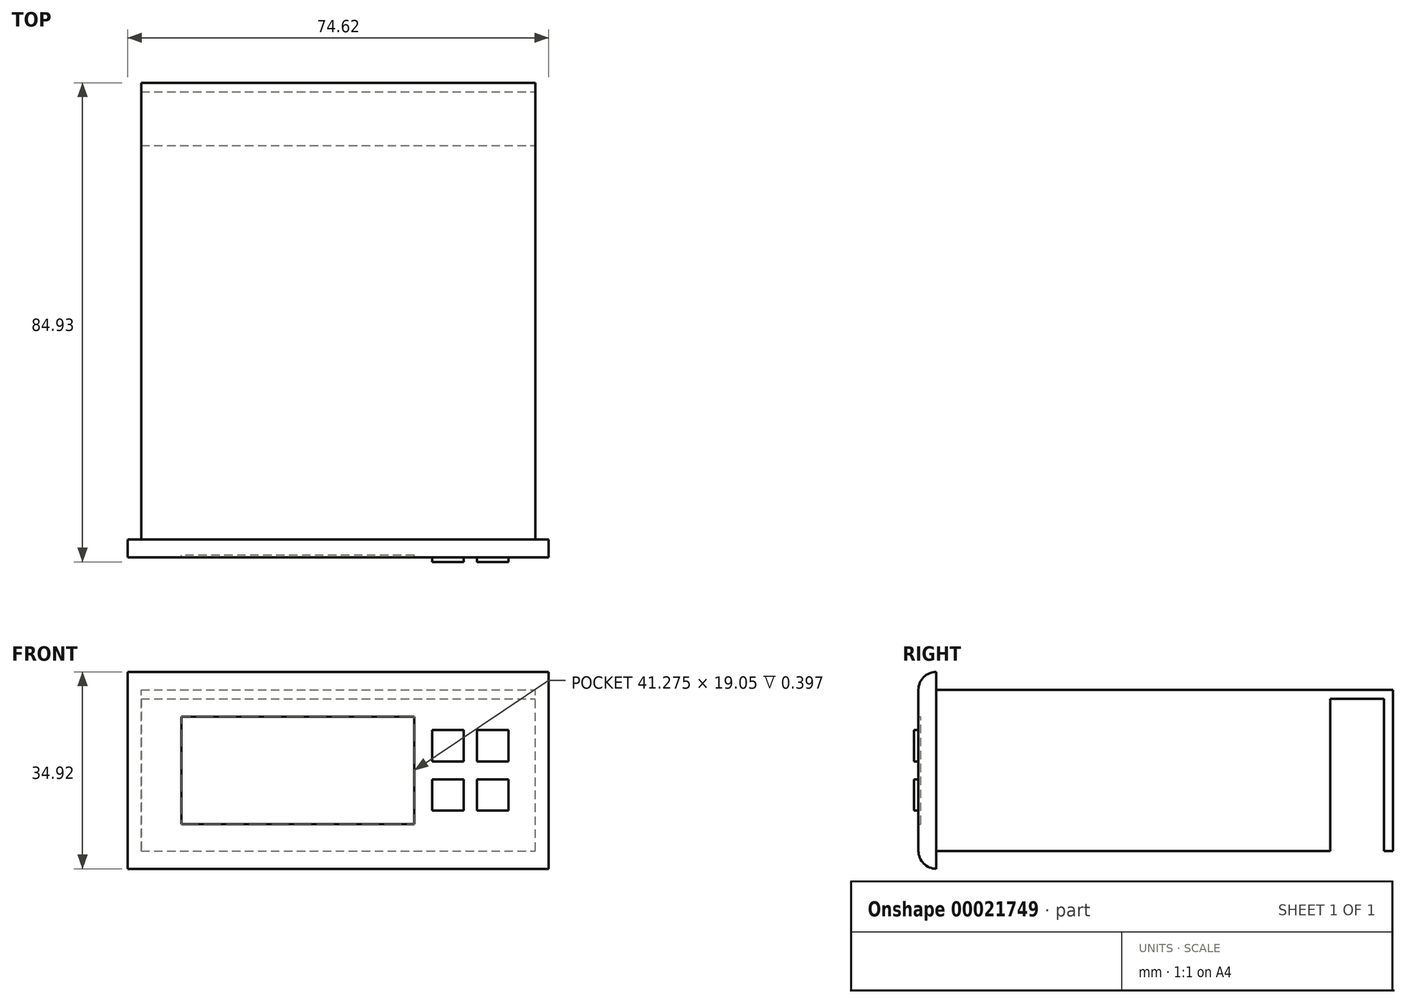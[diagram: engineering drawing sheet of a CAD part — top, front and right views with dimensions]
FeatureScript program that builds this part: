
annotation { "Feature Type Name" : "Feature", "Feature Type Description" : "" }
export const myFeature = defineFeature(function(context is Context, id is Id, definition is map)
    precondition{}
    {
        {
            var Q0;
            Q0=qCreatedBy(makeId("Front.planeOp"),FACE);
            var sketch = newSketch(context, id + "F0", { "sketchPlane" : qUnion([Q0])});
            skLineSegment(sketch, "E0.rect.bottom", {"start": v(37.3, 17.46) * mm, "end": v(-37.3, 17.46) * mm});
            skLineSegment(sketch, "E0.rect.top", {"start": v(37.3, -17.46) * mm, "end": v(-37.3, -17.46) * mm});
            skLineSegment(sketch, "E0.rect.left", {"start": v(37.3, 17.46) * mm, "end": v(37.3, -17.46) * mm});
            skLineSegment(sketch, "E0.rect.right", {"start": v(-37.3, 17.46) * mm, "end": v(-37.3, -17.46) * mm});
            skPoint(sketch, "E0.rect.middle", {"position": v(0, 0) * mm});
            skSolve(sketch);
        }
        {
            var Q0;
            Q0 = qSketchRegion(id + "F0", true);
            extrude(context, id + "F1", {"entities" : qUnion([Q0]), "oppositeDirection" : true, "depth" : 3.17 * mm});
        }
        {
            var Q0;
            Q0=makeQuery(id+"F1.opExtrude","CAP_FACE",FACE,{"disambiguationData":[OSD([sQuery(id+"F0.wireOp",EDGE,"E0.rect.bottom"),sQuery(id+"F0.wireOp",EDGE,"E0.rect.top"),sQuery(id+"F0.wireOp",EDGE,"E0.rect.left"),sQuery(id+"F0.wireOp",EDGE,"E0.rect.right")])],"isStart":false});
            var sketch = newSketch(context, id + "F2", { "sketchPlane" : qUnion([Q0])});
            skLineSegment(sketch, "E1.rect.bottom", {"start": v(34.93, -14.29) * mm, "end": v(-34.93, -14.29) * mm});
            skLineSegment(sketch, "E1.rect.top", {"start": v(34.93, 14.29) * mm, "end": v(-34.93, 14.29) * mm});
            skLineSegment(sketch, "E1.rect.left", {"start": v(34.93, -14.29) * mm, "end": v(34.93, 14.29) * mm});
            skLineSegment(sketch, "E1.rect.right", {"start": v(-34.93, -14.29) * mm, "end": v(-34.93, 14.29) * mm});
            skPoint(sketch, "E1.rect.middle", {"position": v(0, 0) * mm});
            skSolve(sketch);
        }
        {
            var Q0;
            Q0=makeQuery(id+"F2.imprint","IMPRINT",FACE,{"disambiguationData":[TD([[makeQuery(id+"F2.imprint","IMPRINT",EDGE,{"derivedFrom":sQuery(id+"F2.wireOp",EDGE,"E1.rect.bottom")}),-1.0]])]});
            extrude(context, id + "F3", {"entities" : qUnion([Q0]), "operationType" : NewBodyOperationType.ADD, "depth" : 80.96 * mm});
        }
        {
            var Q0;
            Q0=makeQuery(id+"F1.opExtrude","CAP_EDGE",EDGE,{"disambiguationData":[OSD([sQuery(id+"F0.wireOp",EDGE,"E0.rect.bottom")])],"isStart":true});
            var Q1;
            Q1=makeQuery(id+"F1.opExtrude","CAP_EDGE",EDGE,{"disambiguationData":[OSD([sQuery(id+"F0.wireOp",EDGE,"E0.rect.top")])],"isStart":true});
            fillet(context, id + "F4", {"entities" : qUnion([Q0, Q1]), "radius" : 3.17 * mm, "tangentPropagation" : true, "allowEdgeOverflow" : false});
        }
        {
            var Q0;
            Q0=makeQuery(id+"F1.opExtrude","CAP_FACE",FACE,{"disambiguationData":[OSD([sQuery(id+"F0.wireOp",EDGE,"E0.rect.bottom"),sQuery(id+"F0.wireOp",EDGE,"E0.rect.top"),sQuery(id+"F0.wireOp",EDGE,"E0.rect.left"),sQuery(id+"F0.wireOp",EDGE,"E0.rect.right")])],"isStart":true});
            var sketch = newSketch(context, id + "F5", { "sketchPlane" : qUnion([Q0])});
            skLineSegment(sketch, "E2.rect.bottom", {"start": v(13.5, -9.52) * mm, "end": v(-27.78, -9.52) * mm});
            skLineSegment(sketch, "E2.rect.top", {"start": v(13.5, 9.53) * mm, "end": v(-27.78, 9.53) * mm});
            skLineSegment(sketch, "E2.rect.left", {"start": v(13.5, -9.52) * mm, "end": v(13.5, 9.53) * mm});
            skLineSegment(sketch, "E2.rect.right", {"start": v(-27.78, -9.52) * mm, "end": v(-27.78, 9.53) * mm});
            skPoint(sketch, "E2.rect.middle", {"position": v(-7.14, 0) * mm});
            skSolve(sketch);
        }
        {
            var Q0;
            Q0 = qSketchRegion(id + "F5", true);
            extrude(context, id + "F6", {"entities" : qUnion([Q0]), "operationType" : NewBodyOperationType.REMOVE, "oppositeDirection" : true, "depth" : 0.4 * mm});
        }
        {
            var Q0;
            Q0=makeQuery(id+"F1.opExtrude","CAP_FACE",FACE,{"disambiguationData":[OSD([sQuery(id+"F0.wireOp",EDGE,"E0.rect.bottom"),sQuery(id+"F0.wireOp",EDGE,"E0.rect.top"),sQuery(id+"F0.wireOp",EDGE,"E0.rect.left"),sQuery(id+"F0.wireOp",EDGE,"E0.rect.right")])],"isStart":true});
            var sketch = newSketch(context, id + "F7", { "sketchPlane" : qUnion([Q0])});
            skLineSegment(sketch, "E3.rect.bottom", {"start": v(22.23, 1.59) * mm, "end": v(16.67, 1.59) * mm});
            skLineSegment(sketch, "E3.rect.top", {"start": v(22.23, 7.14) * mm, "end": v(16.67, 7.14) * mm});
            skLineSegment(sketch, "E3.rect.left", {"start": v(22.23, 1.59) * mm, "end": v(22.23, 7.14) * mm});
            skLineSegment(sketch, "E3.rect.right", {"start": v(16.67, 1.59) * mm, "end": v(16.67, 7.14) * mm});
            skPoint(sketch, "E3.rect.middle", {"position": v(19.45, 4.37) * mm});
            skLineSegment(sketch, "E4.1.0.0", {"start": v(24.6, 1.59) * mm, "end": v(24.6, 7.14) * mm});
            skLineSegment(sketch, "E4.1.0.1", {"start": v(30.16, 1.59) * mm, "end": v(24.6, 1.59) * mm});
            skLineSegment(sketch, "E4.1.0.2", {"start": v(30.16, 1.59) * mm, "end": v(30.16, 7.14) * mm});
            skLineSegment(sketch, "E4.1.0.3", {"start": v(30.16, 7.14) * mm, "end": v(24.6, 7.14) * mm});
            skLineSegment(sketch, "E4.direction1", {"start": v(16.67, 1.59) * mm, "end": v(22.23, 1.59) * mm, "construction": true});
            skLineSegment(sketch, "E5.MirrorCS", {"start": v(16.67, -1.59) * mm, "end": v(16.67, -7.14) * mm});
            skLineSegment(sketch, "E6.MirrorCS", {"start": v(22.23, -7.14) * mm, "end": v(16.67, -7.14) * mm});
            skLineSegment(sketch, "E7.MirrorCS", {"start": v(22.23, -1.59) * mm, "end": v(16.67, -1.59) * mm});
            skLineSegment(sketch, "E8.MirrorCS", {"start": v(30.16, -7.14) * mm, "end": v(24.6, -7.14) * mm});
            skLineSegment(sketch, "E9.MirrorCS", {"start": v(16.67, -7.14) * mm, "end": v(16.67, -1.59) * mm});
            skLineSegment(sketch, "E10.MirrorCS", {"start": v(22.23, -1.59) * mm, "end": v(22.23, -7.14) * mm});
            skLineSegment(sketch, "E11.MirrorCS", {"start": v(30.16, -1.59) * mm, "end": v(24.6, -1.59) * mm});
            skLineSegment(sketch, "E12.MirrorCS", {"start": v(30.16, -7.14) * mm, "end": v(30.16, -1.59) * mm});
            skLineSegment(sketch, "E13.MirrorCS", {"start": v(24.6, -1.59) * mm, "end": v(24.6, -7.14) * mm});
            skLineSegment(sketch, "E14.MirrorCS", {"start": v(16.67, -1.59) * mm, "end": v(22.23, -1.59) * mm});
            skPoint(sketch, "E15.MirrorP", {"position": v(19.45, -4.37) * mm});
            skSolve(sketch);
        }
        {
            var Q0;
            Q0=makeQuery(id+"F7.imprint","IMPRINT",FACE,{"disambiguationData":[TD([[makeQuery(id+"F7.imprint","IMPRINT",EDGE,{"derivedFrom":sQuery(id+"F7.wireOp",EDGE,"E3.rect.bottom")}),-1.0]])]});
            var Q1;
            Q1=makeQuery(id+"F7.imprint","IMPRINT",FACE,{"disambiguationData":[TD([[makeQuery(id+"F7.imprint","IMPRINT",EDGE,{"derivedFrom":sQuery(id+"F7.wireOp",EDGE,"E4.1.0.0")}),-1.0]])]});
            var Q2;
            Q2=makeQuery(id+"F7.imprint","IMPRINT",FACE,{"disambiguationData":[TD([[makeQuery(id+"F7.imprint","IMPRINT",EDGE,{"derivedFrom":sQuery(id+"F7.wireOp",EDGE,"E8.MirrorCS")}),-1.0]])]});
            var Q3;
            Q3=makeQuery(id+"F7.imprint","IMPRINT",FACE,{"disambiguationData":[TD([[makeQuery(id+"F7.imprint","IMPRINT",EDGE,{"derivedFrom":sQuery(id+"F7.wireOp",EDGE,"E6.MirrorCS")}),-1.0]])]});
            extrude(context, id + "F8", {"entities" : qUnion([Q0, Q1, Q2, Q3]), "operationType" : NewBodyOperationType.ADD, "depth" : 0.8 * mm});
        }
        {
            var Q0;
            Q0=makeQuery(id+"F6.boolean.opBoolean","COPY",FACE,{"derivedFrom":makeQuery(id+"F6.opExtrude","CAP_FACE",FACE,{"disambiguationData":[OSD([sQuery(id+"F5.wireOp",EDGE,"E2.rect.bottom"),sQuery(id+"F5.wireOp",EDGE,"E2.rect.top"),sQuery(id+"F5.wireOp",EDGE,"E2.rect.left"),sQuery(id+"F5.wireOp",EDGE,"E2.rect.right")])],"isStart":false})});
            var Q1;
            Q1=makeQuery(id+"F1.opExtrude","CAP_FACE",FACE,{"disambiguationData":[OSD([sQuery(id+"F0.wireOp",EDGE,"E0.rect.bottom"),sQuery(id+"F0.wireOp",EDGE,"E0.rect.top"),sQuery(id+"F0.wireOp",EDGE,"E0.rect.left"),sQuery(id+"F0.wireOp",EDGE,"E0.rect.right")])],"isStart":true});
            extrude(context, id + "F9", {"entities" : qUnion([Q0]), "endBound" : BoundingType.UP_TO_SURFACE, "endBoundEntityFace" : qUnion([Q1]), "depth" : 25.4 * mm});
        }
        {
            var Q0;
            Q0=makeQuery(id+"F3.opExtrude","SWEPT_FACE",FACE,{"disambiguationData":[OSD([sQuery(id+"F2.wireOp",EDGE,"E1.rect.right")])]});
            var sketch = newSketch(context, id + "F10", { "sketchPlane" : qUnion([Q0])});
            skLineSegment(sketch, "E16.bottom", {"start": v(82.55, -14.29) * mm, "end": v(73.02, -14.29) * mm});
            skLineSegment(sketch, "E16.top", {"start": v(82.55, 12.7) * mm, "end": v(73.02, 12.7) * mm});
            skLineSegment(sketch, "E16.left", {"start": v(82.55, -14.29) * mm, "end": v(82.55, 12.7) * mm});
            skLineSegment(sketch, "E16.right", {"start": v(73.02, -14.29) * mm, "end": v(73.02, 12.7) * mm});
            skSolve(sketch);
        }
        {
            var Q0;
            Q0=makeQuery(id+"F10.imprint","IMPRINT",FACE,{"disambiguationData":[TD([[makeQuery(id+"F10.imprint","IMPRINT",EDGE,{"derivedFrom":sQuery(id+"F10.wireOp",EDGE,"E16.bottom")}),-1.0]])]});
            extrude(context, id + "F11", {"entities" : qUnion([Q0]), "operationType" : NewBodyOperationType.REMOVE, "endBound" : BoundingType.UP_TO_NEXT, "oppositeDirection" : true, "depth" : 25.4 * mm});
        }
    });
